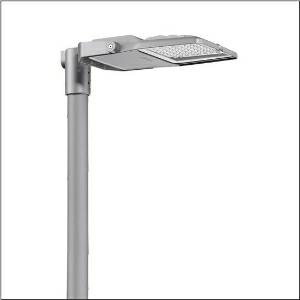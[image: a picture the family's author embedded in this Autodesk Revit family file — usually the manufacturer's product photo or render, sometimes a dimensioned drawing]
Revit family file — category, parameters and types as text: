
# Revit family: floodlight_fl_21_mini___pl64_5xa7776b4e3a_6864
name_source: partatom
category: Lighting Fixtures
units: mm (PartAtom-declared; Revit-internal decimal feet)

## family parameters
Cut with Voids When Loaded = No
Host = Face
Light Source = No
Part Type = Normal
Room Calculation Point = No
Round Connector Dimension = Use Diameter
Shared = No

## types (1)
- --- (1 x LED, 6260 lm, 45.7 W, 4000K)
    Apparent Load = 46 VA
    CIE Flux Codes = 28 80 98 100 100
    Color Rendering = 70
    Color Temperature = 4000K
    Default Elevation = 1800 mm
    Description = Floodlight FL 21 mini, floodlight, primary light control with lens, of PMMA, primary optical cover: protective disc, of toughened safety glass, transparent, light distribution: PL64, light emission: direct distribution, installation type: surface-mounted, LED, High Power LED, rated luminous flux: 6.260lm, luminous efficacy: 137lm/W, light colour: 740, colour temperature: 4000K, control gear: D4iSmart Interface (Zhaga), control: overheat protection, constant luminous flux control, time-dependent luminous flux control, flexible luminous flux parameterisation, pre-setting: logarithmic dimming characteristic, with terminal, 6-pole, mains connection: 220..240V, AC, 50/60Hz, start of lifetime: 46W, end of service life: 48W, reduction: 22W, mast bracket, of diecast aluminium, powder-coated, SITECO metallic grey (DB 702S), corrosivity category C5 mid according to DIN EN ISO 12944, suitable for swimming pools, chlorine-resistant, sealing non-destructively replaceable, mast bracket, of steel, galvanised, powder-coated, SITECO metallic grey (DB 702S), Smart Interface below and above, protection rating (complete): IP66, insulation class (complete): insulation class II (safety insulation), certification: CE, ENEC, VDE, protection symbol: D, impact resistance: IK08, permissible operating ambient temperature: -40..+40°C, permissible operating ambient temperature for outdoor applications: -40..+50°C, standard: DIN EN 12944, LABS conformity tested according to VDMA 24364:2018-05, packaging unit: 1 piece

Light Distribution: PL64
    Height = 70 mm
    Lamp = 1 x LED
    Lamp Light Flux = 6260 lm
    Lamp Power = 45.7 W
    Lamp count = 1
    Length = 485 mm
    Luminous efficacy = 137 lm/W
    Manufacturer = Siteco
    ModVariant = No
    Model = 5XA7776B4E3A
    Number of Poles = 1
    OnlyDefault = Yes
    Power Factor = 1
    Product Name = Floodlight FL 21 mini | PL64
    Product group = floodlight | pylon annexe
    ProductGroupID = 6201
    Protection Class = Protection class II
    Protection Degree = IP 66
    RLX_Detail_Level = 1
    RLX_Emergency_Light_Flux = 0 lm
    RLX_Emergency_Type = 0
    RLX_Emergency_Type_DB = No
    RlxData = <blob elided: 101017 chars, md5=d8a30333>
    Socket = socket
    Standby Power = 0 W
    System Light Flux = 6260 lm
    System Power = 46 W
    Type Comments = factory setting: luminous flux: 100 % | dim-lin: 254 | 463 mA
    Type Image = l_1007125.jpg
    URL = http://relux.com
    VarID = @adj_100045
    Voltage = 0 V
    Weight = 0.00 kg
    Width = 337 mm

## geometry (parser evidence)
native form markers: Blend x4, Sweep x12
no freeform markers — native parametric forms only
